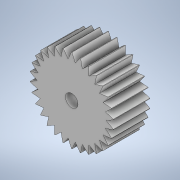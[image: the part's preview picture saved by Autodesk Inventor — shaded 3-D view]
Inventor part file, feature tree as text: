
AUTODESK INVENTOR PART (.ipt)
format: ipt  version: 2022 (Build 260153000, 153)  size: 227,328 bytes
history: native  units: mm
features: sketch x3, extrude x2, hole x1
ambient origin geometry x8: Origin, YZ Plane, XZ Plane, XY Plane, X Axis, Y Axis, Z Axis, Center Point
bodies: Solid1 (feature_tree)
feature tree (6):
  extrude  "Extrusion1"  Depth=17.5mm TaperAngle=0.0deg
  extrude  "Extrusion2"  Depth=10.0mm TaperAngle=0.0deg
  hole  "Hole1"  [1 undecoded]
  sketch  "Sketch1"  dims[d0=40.1mm d1=17.5mm d2=0.0mm]
  sketch  "Sketch2"  dims[d3=300.0mm d5=360.0deg d7=10.0mm d8=0.0mm]
  sketch  "Sketch3"  dims[d9=6.0mm d10=6.0mm d11=4.0mm d12=2.0mm d13=90.0deg d14=8.0mm d15=20.594885mm]
note: 1 required parameter value undecoded (feature->parameter linkage not recoverable at this tier; creation-order binding heuristic only, values carry confidence <= 0.55)
